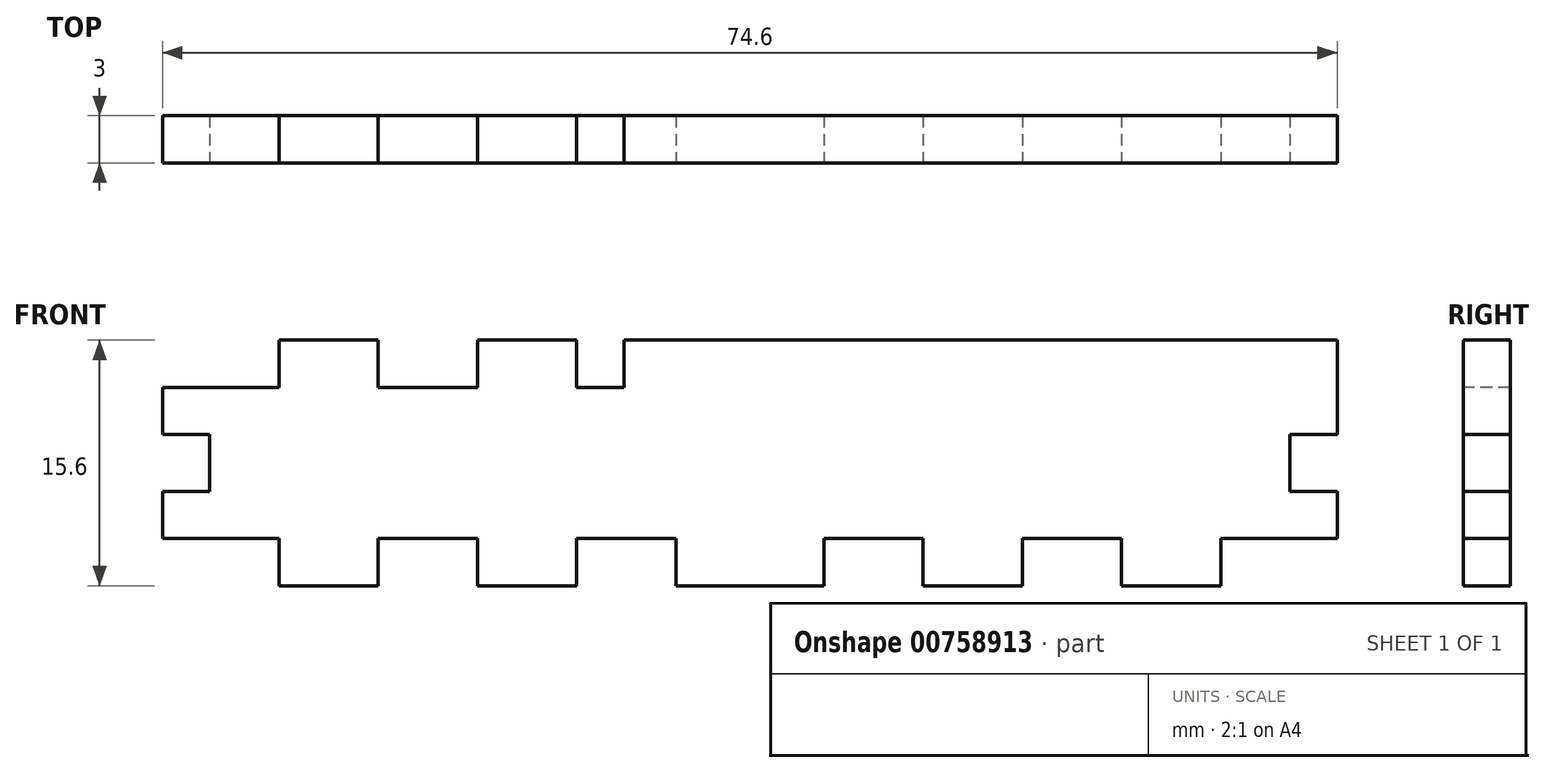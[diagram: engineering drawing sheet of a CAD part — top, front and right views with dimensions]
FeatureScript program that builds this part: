
annotation { "Feature Type Name" : "Feature", "Feature Type Description" : "" }
export const myFeature = defineFeature(function(context is Context, id is Id, definition is map)
    precondition{}
    {
        {
            var Q0;
            Q0=qCreatedBy(makeId("Front.planeOp"),FACE);
            var sketch = newSketch(context, id + "F0", { "sketchPlane" : qUnion([Q0])});
            skLineSegment(sketch, "E0", {"start": v(0, -3) * mm, "end": v(7.4, -3) * mm});
            skLineSegment(sketch, "E1", {"start": v(7.4, -3) * mm, "end": v(7.4, 0) * mm});
            skLineSegment(sketch, "E2", {"start": v(7.4, 0) * mm, "end": v(13.7, 0) * mm});
            skLineSegment(sketch, "E3", {"start": v(13.7, 0) * mm, "end": v(13.7, -3) * mm});
            skLineSegment(sketch, "E4", {"start": v(13.7, -3) * mm, "end": v(20, -3) * mm});
            skLineSegment(sketch, "E5", {"start": v(20, -3) * mm, "end": v(20, 0) * mm});
            skLineSegment(sketch, "E6", {"start": v(20, 0) * mm, "end": v(26.3, 0) * mm});
            skLineSegment(sketch, "E7", {"start": v(26.3, 0) * mm, "end": v(26.3, -3) * mm});
            skLineSegment(sketch, "E8", {"start": v(26.3, -3) * mm, "end": v(29.3, -3) * mm});
            skLineSegment(sketch, "E9", {"start": v(74.6, -6) * mm, "end": v(71.6, -6) * mm});
            skLineSegment(sketch, "E10", {"start": v(71.6, -6) * mm, "end": v(71.6, -9.6) * mm});
            skLineSegment(sketch, "E11", {"start": v(71.6, -9.6) * mm, "end": v(74.6, -9.6) * mm});
            skLineSegment(sketch, "E12", {"start": v(74.6, -9.6) * mm, "end": v(74.6, -12.6) * mm});
            skLineSegment(sketch, "E13", {"start": v(74.6, -12.6) * mm, "end": v(67.2, -12.6) * mm});
            skLineSegment(sketch, "E14", {"start": v(67.2, -12.6) * mm, "end": v(67.2, -15.6) * mm});
            skLineSegment(sketch, "E15", {"start": v(67.2, -15.6) * mm, "end": v(60.9, -15.6) * mm});
            skLineSegment(sketch, "E16", {"start": v(60.9, -15.6) * mm, "end": v(60.9, -12.6) * mm});
            skLineSegment(sketch, "E17", {"start": v(60.9, -12.6) * mm, "end": v(54.6, -12.6) * mm});
            skLineSegment(sketch, "E18", {"start": v(54.6, -12.6) * mm, "end": v(54.6, -15.6) * mm});
            skLineSegment(sketch, "E19", {"start": v(54.6, -15.6) * mm, "end": v(48.3, -15.6) * mm});
            skLineSegment(sketch, "E20", {"start": v(48.3, -15.6) * mm, "end": v(48.3, -12.6) * mm});
            skLineSegment(sketch, "E21", {"start": v(48.3, -12.6) * mm, "end": v(42, -12.6) * mm});
            skLineSegment(sketch, "E22", {"start": v(42, -12.6) * mm, "end": v(42, -15.6) * mm});
            skLineSegment(sketch, "E23", {"start": v(0, -3) * mm, "end": v(0, -6) * mm});
            skLineSegment(sketch, "E24", {"start": v(0, -6) * mm, "end": v(3, -6) * mm});
            skLineSegment(sketch, "E25", {"start": v(3, -6) * mm, "end": v(3, -9.6) * mm});
            skLineSegment(sketch, "E26", {"start": v(3, -9.6) * mm, "end": v(0, -9.6) * mm});
            skLineSegment(sketch, "E27", {"start": v(0, -9.6) * mm, "end": v(0, -12.6) * mm});
            skLineSegment(sketch, "E28", {"start": v(0, -12.6) * mm, "end": v(7.4, -12.6) * mm});
            skLineSegment(sketch, "E29", {"start": v(7.4, -12.6) * mm, "end": v(7.4, -15.6) * mm});
            skLineSegment(sketch, "E30", {"start": v(7.4, -15.6) * mm, "end": v(13.7, -15.6) * mm});
            skLineSegment(sketch, "E31", {"start": v(13.7, -15.6) * mm, "end": v(13.7, -12.6) * mm});
            skLineSegment(sketch, "E32", {"start": v(13.7, -12.6) * mm, "end": v(20, -12.6) * mm});
            skLineSegment(sketch, "E33", {"start": v(20, -12.6) * mm, "end": v(20, -15.6) * mm});
            skLineSegment(sketch, "E34", {"start": v(20, -15.6) * mm, "end": v(26.3, -15.6) * mm});
            skLineSegment(sketch, "E35", {"start": v(26.3, -15.6) * mm, "end": v(26.3, -12.6) * mm});
            skLineSegment(sketch, "E36", {"start": v(26.3, -12.6) * mm, "end": v(32.6, -12.6) * mm});
            skLineSegment(sketch, "E37", {"start": v(32.6, -12.6) * mm, "end": v(32.6, -15.6) * mm});
            skLineSegment(sketch, "E38", {"start": v(32.6, -15.6) * mm, "end": v(42, -15.6) * mm});
            skLineSegment(sketch, "E39", {"start": v(29.3, -3) * mm, "end": v(29.3, 0) * mm});
            skLineSegment(sketch, "E40", {"start": v(29.3, 0) * mm, "end": v(74.6, 0) * mm});
            skLineSegment(sketch, "E41", {"start": v(74.6, 0) * mm, "end": v(74.6, -6) * mm});
            skSolve(sketch);
        }
        {
            var Q0;
            Q0 = qSketchRegion(id + "F0", true);
            extrude(context, id + "F1", {"entities" : qUnion([Q0]), "oppositeDirection" : true, "depth" : 3 * mm, "offsetDistance" : 25 * mm});
        }
    });
